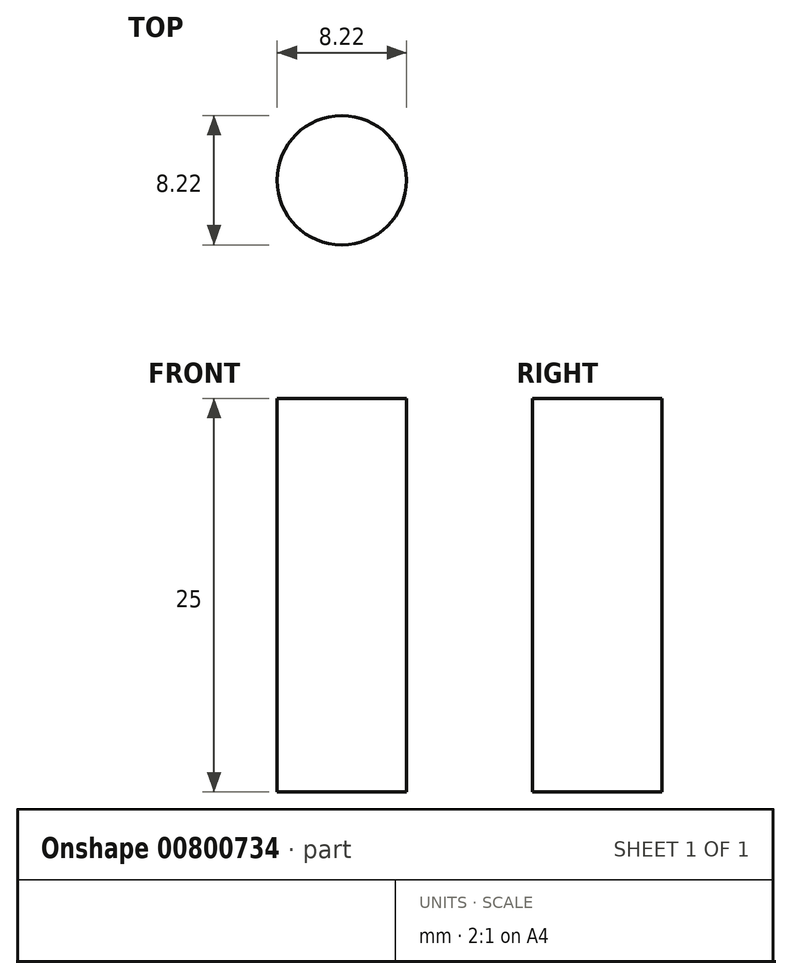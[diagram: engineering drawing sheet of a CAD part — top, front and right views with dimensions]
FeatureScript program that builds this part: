
annotation { "Feature Type Name" : "Feature", "Feature Type Description" : "" }
export const myFeature = defineFeature(function(context is Context, id is Id, definition is map)
    precondition{}
    {
        {
            var Q0;
            Q0=qCreatedBy(makeId("Front.planeOp"),FACE);
            var sketch = newSketch(context, id + "F0", { "sketchPlane" : qUnion([Q0])});
            skLineSegment(sketch, "E0", {"start": v(33.56, 0) * mm, "end": v(4.42, 0) * mm});
            skLineSegment(sketch, "E1", {"start": v(4.42, 0) * mm, "end": v(4.42, 30.45) * mm});
            skFitSpline(sketch, "E2", {"points": [v(4.42, 30.45) * mm, v(31.6, 55.67) * mm, v(40.11, 96.92) * mm], "startDerivative": vector(65.74, 45.35) * mm, "endDerivative": vector(6.27, 87.15) * mm});
            skFitSpline(sketch, "E3.0", {"points": [v(6.12, 27.98) * mm, v(8.86, 29.87) * mm, v(14.39, 33.68) * mm, v(21, 38.81) * mm, v(25.88, 43.34) * mm, v(29.27, 46.99) * mm, v(31.8, 50.3) * mm, v(33.6, 53.1) * mm, v(35.27, 56.05) * mm, v(37.01, 59.91) * mm, v(38.67, 64.78) * mm, v(39.96, 69.84) * mm, v(41.27, 76.79) * mm, v(42.32, 85.77) * mm, v(42.84, 93.08) * mm, v(43.1, 96.7) * mm]});
            skLineSegment(sketch, "E3.1", {"start": v(7.42, 3) * mm, "end": v(7.42, 28.88) * mm});
            skLineSegment(sketch, "E3.2", {"start": v(33.56, 3) * mm, "end": v(7.42, 3) * mm});
            skLineSegment(sketch, "E4", {"start": v(43.1, 96.7) * mm, "end": v(40.11, 96.92) * mm});
            skLineSegment(sketch, "E5", {"start": v(33.56, 3) * mm, "end": v(33.56, 0) * mm});
            skLineSegment(sketch, "E6", {"start": v(0, 92.57) * mm, "end": v(0, -10.87) * mm, "construction": true});
            skSolve(sketch);
        }
        {
            var Q0;
            Q0=sQuery(id+"F0.wireOp",EDGE,"E2");
            var Q1;
            Q1=sQuery(id+"F0.wireOp",EDGE,"E4");
            var Q2;
            Q2=sQuery(id+"F0.wireOp",EDGE,"E3.0");
            var Q3;
            Q3=sQuery(id+"F0.wireOp",EDGE,"E1");
            var Q4;
            Q4=sQuery(id+"F0.wireOp",EDGE,"E3.1");
            var Q5;
            Q5=sQuery(id+"F0.wireOp",EDGE,"E3.2");
            var Q6;
            Q6=sQuery(id+"F0.wireOp",EDGE,"E0");
            var Q7;
            Q7=sQuery(id+"F0.wireOp",EDGE,"E5");
            var Q8;
            Q8=sQuery(id+"F0.wireOp",EDGE,"E6");
            revolve(context, id + "F1", {"bodyType" : ToolBodyType.SURFACE, "surfaceOperationType" : NewSurfaceOperationType.NEW, "surfaceEntities" : qUnion([Q0, Q1, Q2, Q3, Q4, Q5, Q6, Q7]), "axis" : qUnion([Q8]), "revolveType" : RevolveType.FULL});
        }
        {
            var Q0;
            Q0=makeQuery(id+"F1.opRevolve","SWEPT_FACE",FACE,{"disambiguationData":[OSD([sQuery(id+"F0.wireOp",EDGE,"E0")])]});
            var sketch = newSketch(context, id + "F2", { "sketchPlane" : qUnion([Q0])});
            skCircle(sketch, "E7", {"center": v(0, 0) * mm, "radius": 4.1 * mm});
            skSolve(sketch);
        }
        {
            var Q0;
            Q0 = qSketchRegion(id + "F2", true);
            extrude(context, id + "F3", {"entities" : qUnion([Q0]), "depth" : 25 * mm, "offsetDistance" : 25 * mm});
        }
    });
